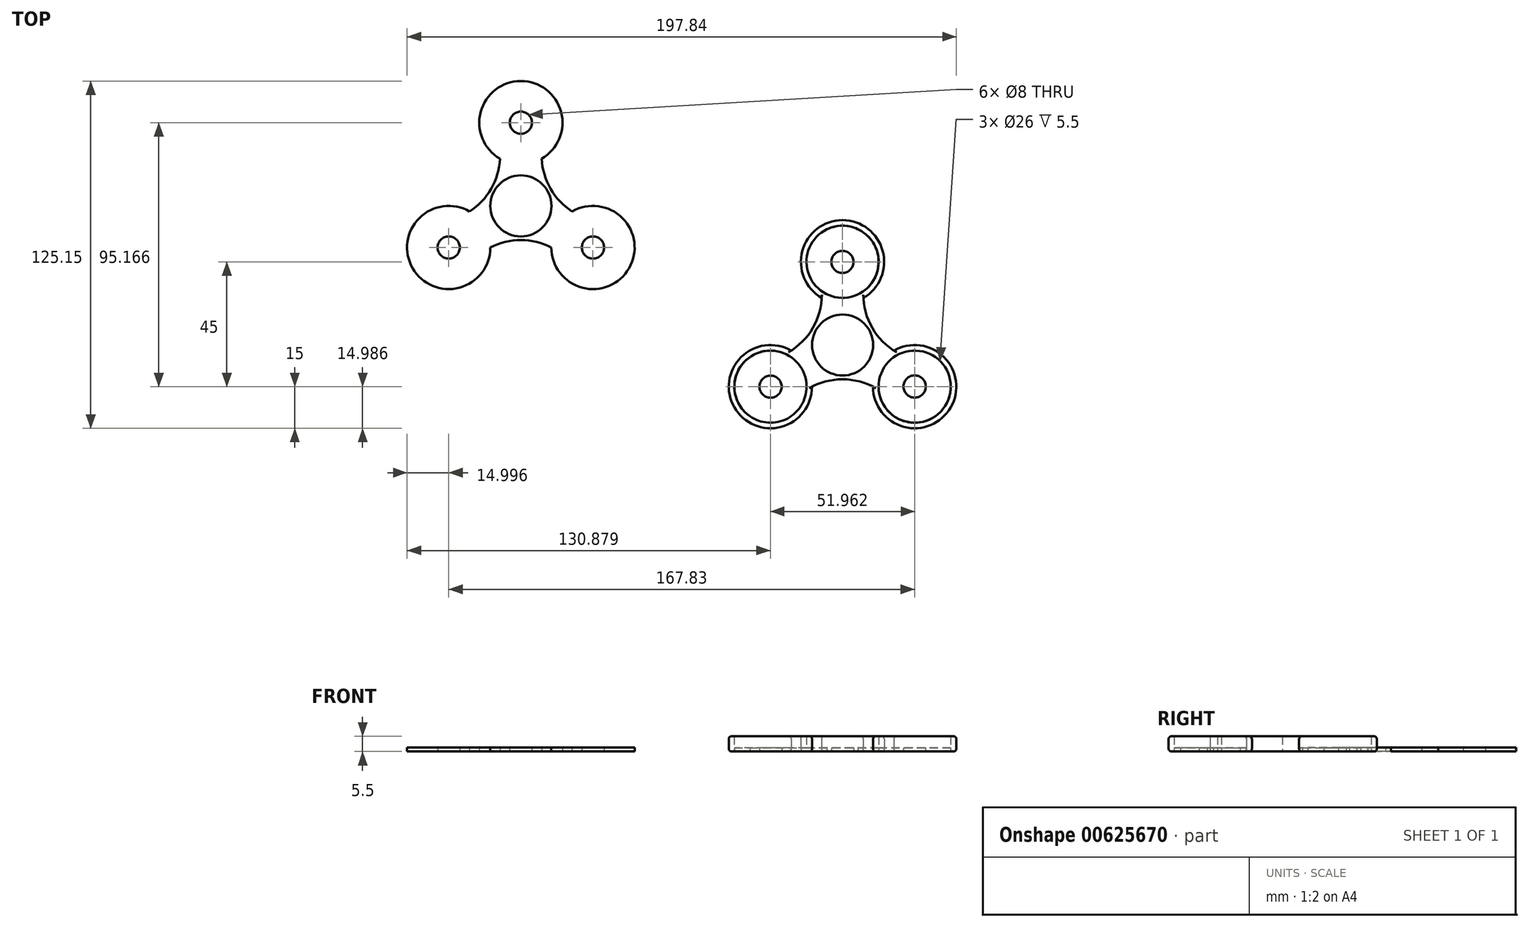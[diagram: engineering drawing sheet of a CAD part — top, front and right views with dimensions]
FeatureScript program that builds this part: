
annotation { "Feature Type Name" : "Feature", "Feature Type Description" : "" }
export const myFeature = defineFeature(function(context is Context, id is Id, definition is map)
    precondition{}
    {
        {
            var Q0;
            Q0=qCreatedBy(makeId("Top.planeOp"),FACE);
            var sketch = newSketch(context, id + "F0", { "sketchPlane" : qUnion([Q0])});
            skCircle(sketch, "E0", {"center": v(0, 0) * mm, "radius": 11.05 * mm, "construction": true});
            skCircle(sketch, "E1", {"center": v(0, 30) * mm, "radius": 13 * mm});
            skCircle(sketch, "E2", {"center": v(0, 30) * mm, "radius": 15 * mm});
            skCircle(sketch, "E3.1.0", {"center": v(-25.98, -15) * mm, "radius": 15 * mm});
            skCircle(sketch, "E3.1.1", {"center": v(-25.98, -15) * mm, "radius": 13 * mm});
            skCircle(sketch, "E3.2.0", {"center": v(25.98, -15) * mm, "radius": 15 * mm});
            skCircle(sketch, "E3.2.1", {"center": v(25.98, -15) * mm, "radius": 13 * mm});
            skLineSegment(sketch, "E4", {"start": v(-25.98, -15) * mm, "end": v(0, 30) * mm, "construction": true});
            skLineSegment(sketch, "E5", {"start": v(0, 30) * mm, "end": v(25.98, -15) * mm, "construction": true});
            skLineSegment(sketch, "E6", {"start": v(25.98, -15) * mm, "end": v(-25.98, -15) * mm, "construction": true});
            skArc(sketch, "E7", {"start": v(-18.48, -2) * mm, "mid": v(-10.7, 6.17) * mm, "end": v(-7.5, 17) * mm});
            skArc(sketch, "E8.MirrorCS", {"start": v(18.48, -2) * mm, "mid": v(10.7, 6.17) * mm, "end": v(7.5, 17) * mm});
            skArc(sketch, "E9", {"start": v(10.98, -15) * mm, "mid": v(0, -12.35) * mm, "end": v(-10.98, -15) * mm});
            skCircle(sketch, "E10", {"center": v(0, 0) * mm, "radius": 11 * mm});
            skSolve(sketch);
        }
        {
            var Q0;
            Q0 = qSketchRegion(id + "F0", true);
            extrude(context, id + "F1", {"entities" : qUnion([Q0]), "depth" : 5.5 * mm, "offsetDistance" : 25 * mm});
        }
        {
            var Q0;
            Q0=makeQuery(id+"F1.opExtrude","CAP_EDGE",EDGE,{"disambiguationData":[OSD([sQuery(id+"F0.wireOp",EDGE,"E3.1.0")])],"isStart":true});
            var Q1;
            Q1=makeQuery(id+"F1.opExtrude","CAP_EDGE",EDGE,{"disambiguationData":[OSD([sQuery(id+"F0.wireOp",EDGE,"E3.2.0")])],"isStart":true});
            var Q2;
            Q2=makeQuery(id+"F1.opExtrude","CAP_EDGE",EDGE,{"disambiguationData":[OSD([sQuery(id+"F0.wireOp",EDGE,"E2")])],"isStart":true});
            var Q3;
            Q3=makeQuery(id+"F1.opExtrude","CAP_EDGE",EDGE,{"disambiguationData":[OSD([sQuery(id+"F0.wireOp",EDGE,"E3.2.0")])],"isStart":false});
            var Q4;
            Q4=makeQuery(id+"F1.opExtrude","CAP_EDGE",EDGE,{"disambiguationData":[OSD([sQuery(id+"F0.wireOp",EDGE,"E3.1.0")])],"isStart":false});
            var Q5;
            Q5=makeQuery(id+"F1.opExtrude","CAP_EDGE",EDGE,{"disambiguationData":[OSD([sQuery(id+"F0.wireOp",EDGE,"E2")])],"isStart":false});
            fillet(context, id + "F2", {"entities" : qUnion([Q0, Q1, Q2, Q3, Q4, Q5]), "radius" : 1 * mm, "tangentPropagation" : true, "allowEdgeOverflow" : false});
        }
        {
            var Q0;
            Q0=qCreatedBy(makeId("Top.planeOp"),FACE);
            var sketch = newSketch(context, id + "F3", { "sketchPlane" : qUnion([Q0])});
            skCircle(sketch, "E11", {"center": v(-115.88, 50.15) * mm, "radius": 11.05 * mm, "construction": true});
            skCircle(sketch, "E12", {"center": v(-115.88, 80.15) * mm, "radius": 15 * mm});
            skCircle(sketch, "E13.1.0", {"center": v(-141.86, 35.15) * mm, "radius": 15 * mm});
            skCircle(sketch, "E13.2.0", {"center": v(-89.9, 35.15) * mm, "radius": 15 * mm});
            skLineSegment(sketch, "E14", {"start": v(-141.86, 35.15) * mm, "end": v(-115.88, 80.15) * mm, "construction": true});
            skLineSegment(sketch, "E15", {"start": v(-115.88, 80.15) * mm, "end": v(-89.9, 35.15) * mm, "construction": true});
            skLineSegment(sketch, "E16", {"start": v(-89.9, 35.15) * mm, "end": v(-141.86, 35.15) * mm, "construction": true});
            skArc(sketch, "E17", {"start": v(-134.36, 48.14) * mm, "mid": v(-126.58, 56.33) * mm, "end": v(-123.38, 67.16) * mm});
            skArc(sketch, "E18.MirrorCS", {"start": v(-97.4, 48.14) * mm, "mid": v(-105.19, 56.33) * mm, "end": v(-108.38, 67.16) * mm});
            skArc(sketch, "E19", {"start": v(-104.9, 35.15) * mm, "mid": v(-115.88, 37.8) * mm, "end": v(-126.86, 35.15) * mm});
            skCircle(sketch, "E20", {"center": v(-115.88, 50.15) * mm, "radius": 11 * mm});
            skCircle(sketch, "E21", {"center": v(-115.88, 80.15) * mm, "radius": 4 * mm});
            skCircle(sketch, "E22", {"center": v(-89.9, 35.15) * mm, "radius": 4 * mm});
            skCircle(sketch, "E23", {"center": v(-141.86, 35.15) * mm, "radius": 4 * mm});
            skSolve(sketch);
        }
        {
            var Q0;
            Q0 = qSketchRegion(id + "F3", true);
            extrude(context, id + "F4", {"entities" : qUnion([Q0]), "depth" : 1.5 * mm, "offsetDistance" : 25 * mm});
        }
        {
            var Q0;
            Q0=qCreatedBy(makeId("Top.planeOp"),FACE);
            var sketch = newSketch(context, id + "F5", { "sketchPlane" : qUnion([Q0])});
            skCircle(sketch, "E24", {"center": v(-0.02, 29.99) * mm, "radius": 13 * mm});
            skCircle(sketch, "E25.1.0", {"center": v(-25.96, -15.01) * mm, "radius": 13 * mm});
            skCircle(sketch, "E25.2.0", {"center": v(25.98, -14.98) * mm, "radius": 13 * mm});
            skPoint(sketch, "E25.center", {"position": v(0, 0) * mm});
            skCircle(sketch, "E26", {"center": v(-25.93, -15.01) * mm, "radius": 4 * mm});
            skCircle(sketch, "E27.1.0", {"center": v(25.97, -14.95) * mm, "radius": 4 * mm});
            skCircle(sketch, "E27.2.0", {"center": v(-0.04, 29.96) * mm, "radius": 4 * mm});
            skSolve(sketch);
        }
        {
            var Q0;
            Q0 = qSketchRegion(id + "F5", true);
            extrude(context, id + "F6", {"entities" : qUnion([Q0]), "operationType" : NewBodyOperationType.ADD, "depth" : 1.3 * mm, "offsetDistance" : 25 * mm});
        }
    });
